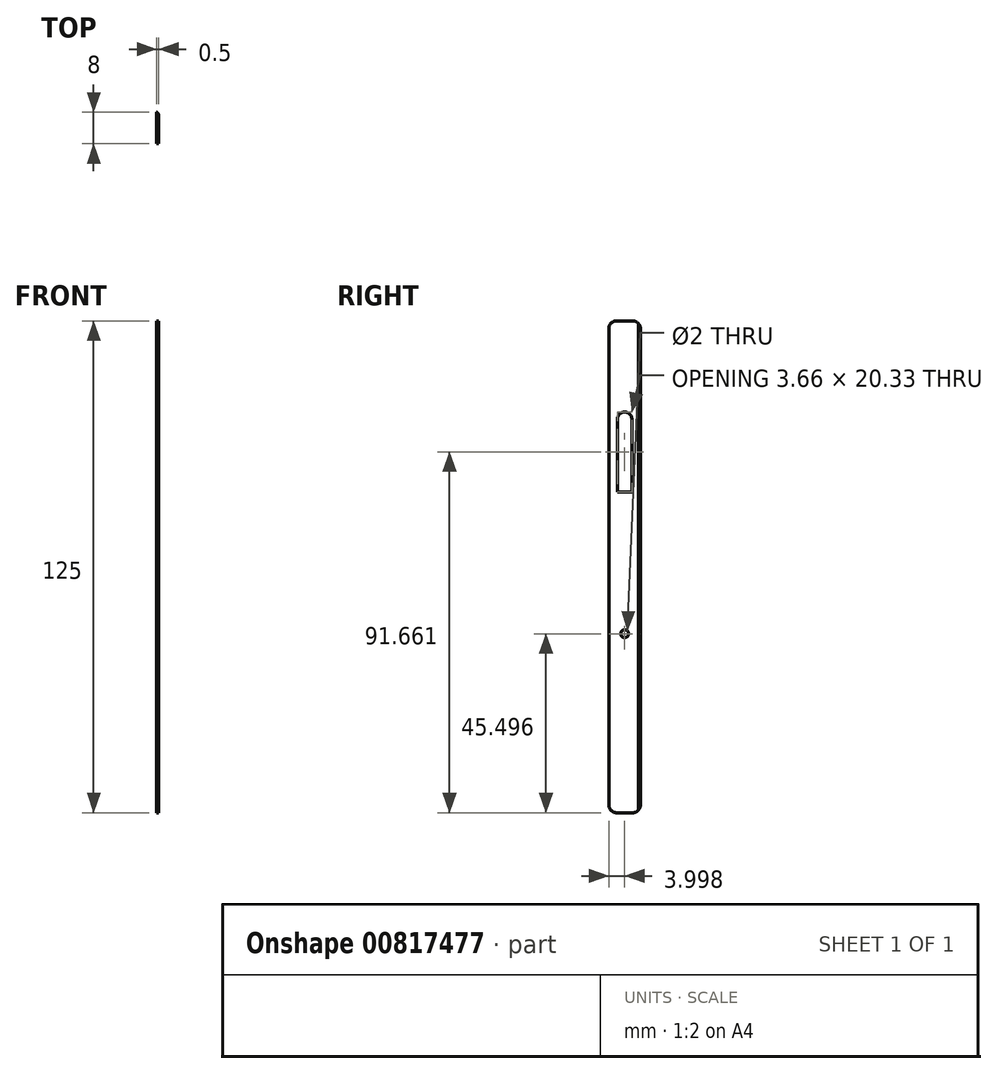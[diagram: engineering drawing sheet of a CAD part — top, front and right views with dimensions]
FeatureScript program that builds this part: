
annotation { "Feature Type Name" : "Feature", "Feature Type Description" : "" }
export const myFeature = defineFeature(function(context is Context, id is Id, definition is map)
    precondition{}
    {
        {
            var Q0;
            Q0=qCreatedBy(makeId("Right.planeOp"),FACE);
            var sketch = newSketch(context, id + "F0", { "sketchPlane" : qUnion([Q0])});
            skLineSegment(sketch, "E0.bottom", {"start": v(26.29, 33.53) * mm, "end": v(34.29, 33.53) * mm});
            skLineSegment(sketch, "E0.top", {"start": v(26.29, 158.53) * mm, "end": v(34.29, 158.53) * mm});
            skLineSegment(sketch, "E0.left", {"start": v(26.29, 33.53) * mm, "end": v(26.29, 158.53) * mm});
            skLineSegment(sketch, "E0.right", {"start": v(34.29, 33.53) * mm, "end": v(34.29, 158.53) * mm});
            skSolve(sketch);
        }
        {
            var Q0;
            Q0=qSketchRegion(id+"F0",true);
            extrude(context, id + "F1", {"entities" : qUnion([Q0]), "depth" : 0.5 * mm, "offsetDistance" : 25 * mm});
        }
        {
            var Q0;
            Q0=makeQuery(id+"F1.opExtrude","SWEPT_EDGE",EDGE,{"disambiguationData":[OSD([sQuery(id+"F0.wireOp",EDGE,"E0.top"),sQuery(id+"F0.wireOp",EDGE,"E0.left")])]});
            var Q1;
            Q1=makeQuery(id+"F1.opExtrude","SWEPT_EDGE",EDGE,{"disambiguationData":[OSD([sQuery(id+"F0.wireOp",EDGE,"E0.top"),sQuery(id+"F0.wireOp",EDGE,"E0.right")])]});
            var Q2;
            Q2=makeQuery(id+"F1.opExtrude","SWEPT_EDGE",EDGE,{"disambiguationData":[OSD([sQuery(id+"F0.wireOp",EDGE,"E0.bottom"),sQuery(id+"F0.wireOp",EDGE,"E0.right")])]});
            var Q3;
            Q3=makeQuery(id+"F1.opExtrude","SWEPT_EDGE",EDGE,{"disambiguationData":[OSD([sQuery(id+"F0.wireOp",EDGE,"E0.bottom"),sQuery(id+"F0.wireOp",EDGE,"E0.left")])]});
            fillet(context, id + "F2", {"entities" : qUnion([Q0, Q1, Q2, Q3]), "radius" : 2 * mm, "tangentPropagation" : true, "allowEdgeOverflow" : false});
        }
        {
            var Q0;
            Q0=makeQuery(id+"F1.opExtrude","CAP_FACE",FACE,{"disambiguationData":[OSD([sQuery(id+"F0.wireOp",EDGE,"E0.bottom"),sQuery(id+"F0.wireOp",EDGE,"E0.top"),sQuery(id+"F0.wireOp",EDGE,"E0.left"),sQuery(id+"F0.wireOp",EDGE,"E0.right")])],"isStart":false});
            var sketch = newSketch(context, id + "F3", { "sketchPlane" : qUnion([Q0])});
            skLineSegment(sketch, "E1", {"start": v(26.29, 135.36) * mm, "end": v(34.29, 135.36) * mm, "construction": true});
            skLineSegment(sketch, "E2", {"start": v(30.29, 152.58) * mm, "end": v(30.29, 95.45) * mm, "construction": true});
            skPoint(sketch, "E3", {"position": v(30.29, 135.36) * mm});
            skLineSegment(sketch, "E4.top", {"start": v(28.46, 115.03) * mm, "end": v(32.12, 115.03) * mm});
            skLineSegment(sketch, "E4.left", {"start": v(28.46, 133.53) * mm, "end": v(28.46, 115.03) * mm});
            skLineSegment(sketch, "E4.right", {"start": v(32.12, 133.53) * mm, "end": v(32.12, 115.03) * mm});
            skPoint(sketch, "E4.middle", {"position": v(30.29, 124.28) * mm});
            skArc(sketch, "E5", {"start": v(32.12, 133.53) * mm, "mid": v(30.29, 135.36) * mm, "end": v(28.46, 133.53) * mm});
            skLineSegment(sketch, "E6", {"start": v(34.29, 79.03) * mm, "end": v(26.29, 79.03) * mm, "construction": true});
            skCircle(sketch, "E7", {"center": v(30.29, 79.03) * mm, "radius": 1 * mm});
            skSolve(sketch);
        }
        {
            var Q0;
            Q0=qSketchRegion(id+"F3",true);
            extrude(context, id + "F4", {"entities" : qUnion([Q0]), "operationType" : NewBodyOperationType.REMOVE, "endBound" : BoundingType.SYMMETRIC, "oppositeDirection" : true, "depth" : 25 * mm, "offsetDistance" : 25 * mm});
        }
        {
            var Q0;
            Q0=makeQuery(id+"F1.opExtrude","CAP_EDGE",EDGE,{"disambiguationData":[OSD([sQuery(id+"F0.wireOp",EDGE,"E0.right")])],"isStart":false});
            chamfer(context, id + "F5", {"entities" : qUnion([Q0]), "chamferType" : ChamferType.OFFSET_ANGLE, "width" : 0.5 * mm, "oppositeDirection" : false, "angle" : 45 * degree});
        }
    });
